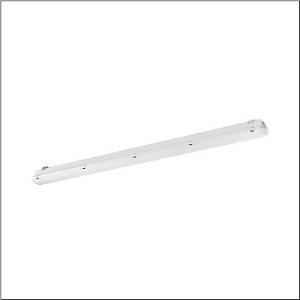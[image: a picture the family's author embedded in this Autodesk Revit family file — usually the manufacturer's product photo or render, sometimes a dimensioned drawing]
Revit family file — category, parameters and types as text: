
# Revit family: monsun_r__11xtreme_ho_51fe10dp480s_3f43
name_source: partatom
category: Lighting Fixtures
units: mm (PartAtom-declared; Revit-internal decimal feet)

## family parameters
Cut with Voids When Loaded = No
Host = Face
Light Source = No
Part Type = Normal
Room Calculation Point = No
Round Connector Dimension = Use Diameter
Shared = No

## types (1)
- --- (1 x LED, 8000 lm, 41 W, 4000K)
    Apparent Load = 41 VA
    CIE Flux Codes = 47 76 93 94 100
    Color Rendering = 80
    Color Temperature = 4000K
    Default Elevation = 1800 mm
    Description = Monsun® 11Xtreme HO, damp-proof luminaire, chain hanger, primary optical cover: enclosure, of PMMA, light emission: direct distribution, primary light characteristic: symmetric, installation type: suspended mounting, surface-mounted, horizontal mounting, vertical mounting, LED, rated luminous flux: 8.000lm, luminous efficacy: 195lm/W, light colour: 840, colour temperature: 4000K, control gear: DALI 2, with terminal, 5-pole, max. 2.5mm², mains connection: 220..240V, AC, 50/60Hz, rated input power: 41W, luminaire housing, of glass-fibre reinforced polyester, uncoated, bright grey, incl. chain hanger, length: 1.590mm, width: 90mm, height: 88mm, clip for enclosure, of stainless steel (V2A), ceiling mounting element, of stainless steel (V2A), chain hanger, of stainless steel (V2A), protection rating (complete): IP66, insulation class (complete): insulation class I (protective earthing), certification: CE, ENEC, VDE, UKCA, protection symbol: D, impact resistance: IK04, permissible operating ambient temperature: -35..+55°C, standard: EN 50419, EN 60598-2-1, contact your sales advisor before using the luminaires in applications with unclear chemical exposure, large temperature fluctuations or condensation-forming humidity, LABS conformity tested according to VDMA 24364:2018-05, no direct snow, no direct sun, no direct rain, for indoor or canopied outdoor use, corresponds to IFS (International Featured Standards) requirements for safety and quality in the food industry, packaging unit: 1 piece
    Height = 88 mm
    Lamp = 1 x LED
    Lamp Light Flux = 8000 lm
    Lamp Power = 41 W
    Lamp count = 1
    Length = 1590 mm
    Luminous efficacy = 195 lm/W
    Manufacturer = Siteco
    ModVariant = No
    Model = 51FE10DP480S
    Mounting Place = Ceiling
    Mounting Type = Surface mounted
    Number of Poles = 1
    OnlyDefault = Yes
    Power Factor = 1
    Product Name = Monsun® 11Xtreme HO
    Product group = damp-proof luminaire
    ProductGroupID = 301
    Protection Class = Protection class I
    Protection Degree = IP 66
    RLX_Detail_Level = 1
    RLX_Emergency_Light_Flux = 0 lm
    RLX_Emergency_Type = 0
    RLX_Emergency_Type_DB = No
    RlxData = <blob elided: 87321 chars, md5=be2f3ba4>
    Socket = socket
    Standby Power = 0 W
    System Light Flux = 8000 lm
    System Power = 41 W
    Type Comments = factory setting: luminous flux: 100 % | dim-lin: 254 | 284 mA
    Type Image = l_1349234.jpg
    URL = http://relux.com
    VarID = @adj_043075
    Voltage = 0 V
    Weight = 0.00 kg
    Width = 90 mm

## geometry (parser evidence)
native form markers: Blend x4, Sweep x14
no freeform markers — native parametric forms only
